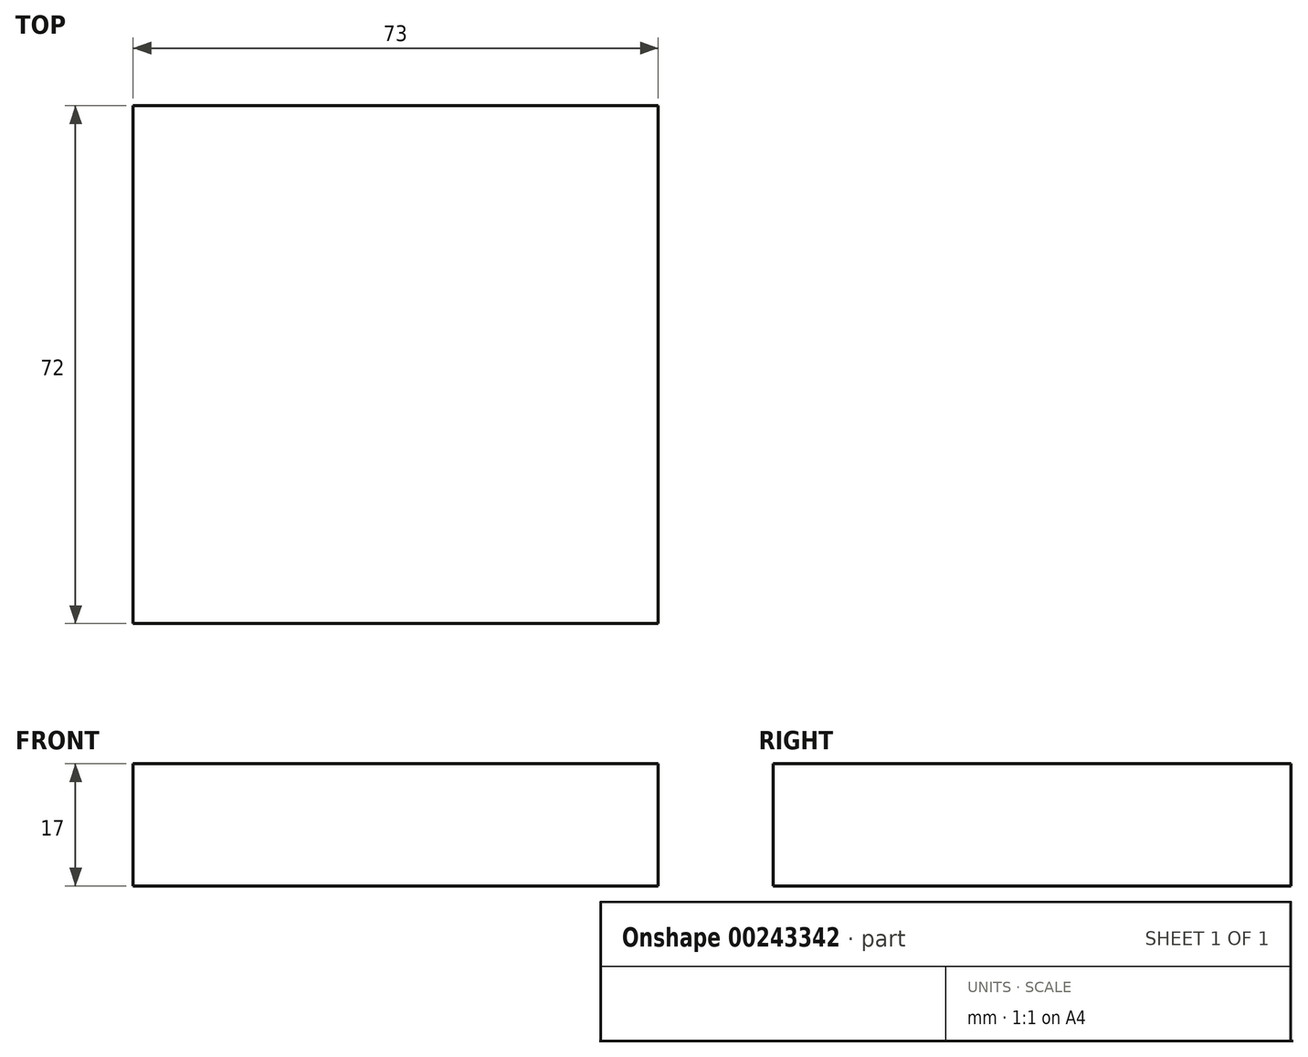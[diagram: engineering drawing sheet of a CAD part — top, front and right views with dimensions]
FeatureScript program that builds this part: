
annotation { "Feature Type Name" : "Feature", "Feature Type Description" : "" }
export const myFeature = defineFeature(function(context is Context, id is Id, definition is map)
    precondition{}
    {
        {
            var Q0;
            Q0=qCreatedBy(makeId("Top.planeOp"),FACE);
            var sketch = newSketch(context, id + "F0", { "sketchPlane" : qUnion([Q0])});
            skLineSegment(sketch, "E0.bottom", {"start": v(-36.5, 36) * mm, "end": v(36.5, 36) * mm});
            skLineSegment(sketch, "E0.top", {"start": v(-36.5, -36) * mm, "end": v(36.5, -36) * mm});
            skLineSegment(sketch, "E0.left", {"start": v(-36.5, 36) * mm, "end": v(-36.5, -36) * mm});
            skLineSegment(sketch, "E0.right", {"start": v(36.5, 36) * mm, "end": v(36.5, -36) * mm});
            skPoint(sketch, "E0.middle", {"position": v(0, 0) * mm});
            skSolve(sketch);
        }
        {
            var Q0;
            Q0 = qSketchRegion(id + "F0", true);
            extrude(context, id + "F1", {"entities" : qUnion([Q0]), "depth" : 17 * mm});
        }
    });
